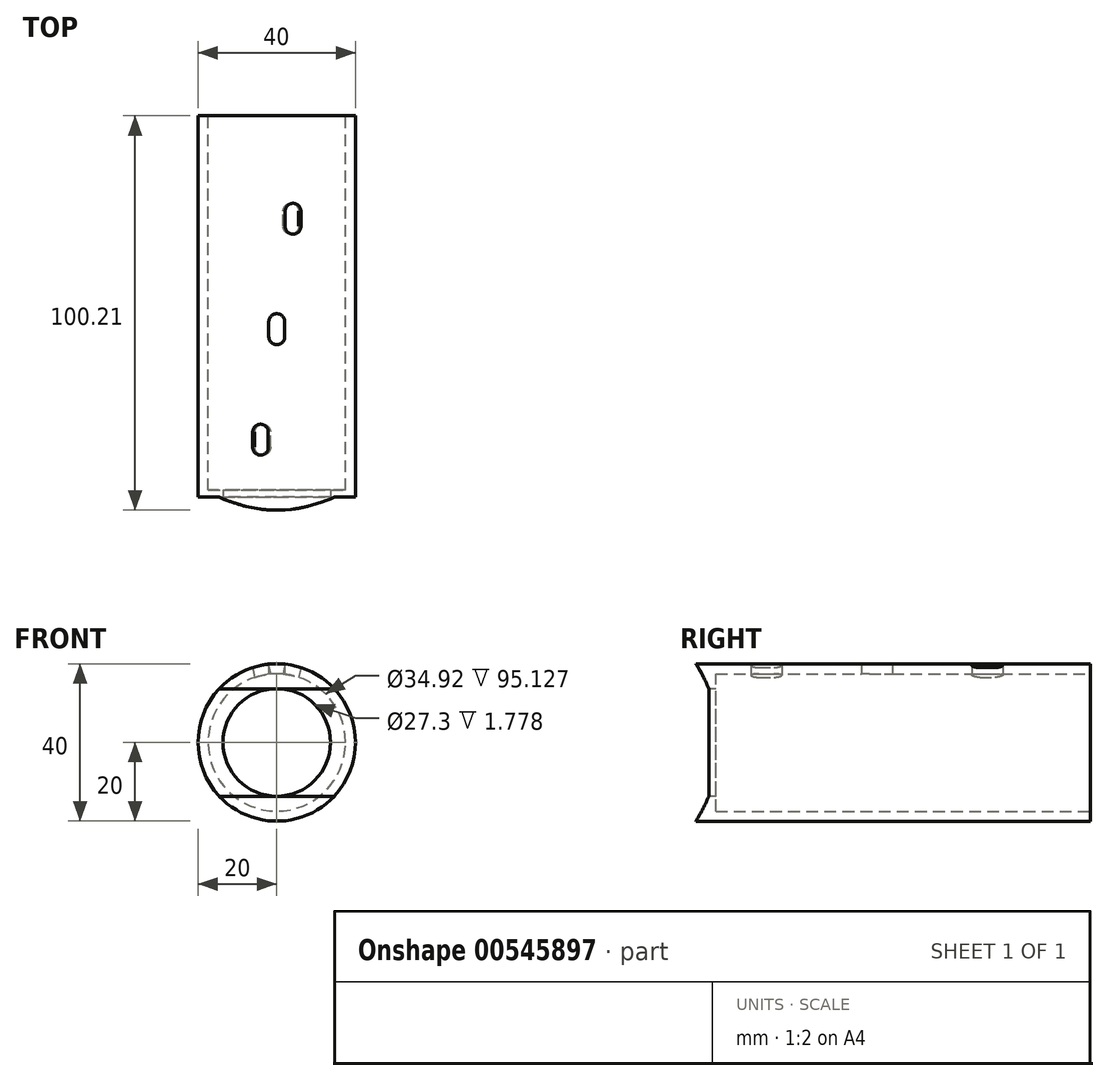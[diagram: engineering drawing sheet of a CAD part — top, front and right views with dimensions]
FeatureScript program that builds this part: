
annotation { "Feature Type Name" : "Feature", "Feature Type Description" : "" }
export const myFeature = defineFeature(function(context is Context, id is Id, definition is map)
    precondition{}
    {
        {
            var Q0;
            Q0=qCreatedBy(makeId("Front.planeOp"),FACE);
            var sketch = newSketch(context, id + "F0", { "sketchPlane" : qUnion([Q0])});
            skCircle(sketch, "E0", {"center": v(0, 0) * mm, "radius": 20 * mm});
            skCircle(sketch, "E1", {"center": v(0, 0) * mm, "radius": 17.46 * mm});
            skSolve(sketch);
        }
        {
            var Q0;
            Q0 = qSketchRegion(id + "F0", true);
            extrude(context, id + "F1", {"entities" : qUnion([Q0]), "endBound" : BoundingType.SYMMETRIC, "depth" : 95 * mm, "offsetDistance" : 25.4 * mm});
        }
        {
            var Q0;
            Q0=makeQuery(id+"F1.opExtrude","CAP_FACE",FACE,{"disambiguationData":[OSD([sQuery(id+"F0.wireOp",EDGE,"E0"),sQuery(id+"F0.wireOp",EDGE,"E1")])],"isStart":false});
            var sketch = newSketch(context, id + "F2", { "sketchPlane" : qUnion([Q0])});
            skCircle(sketch, "E2", {"center": v(0, 0) * mm, "radius": 13.65 * mm});
            skCircle(sketch, "E3.0", {"center": v(0, 0) * mm, "radius": 20 * mm});
            skCircle(sketch, "E4.0", {"center": v(0, 0) * mm, "radius": 17.46 * mm, "construction": true});
            skSolve(sketch);
        }
        {
            var Q0;
            Q0 = qSketchRegion(id + "F2", true);
            extrude(context, id + "F3", {"entities" : qUnion([Q0]), "operationType" : NewBodyOperationType.ADD, "oppositeDirection" : true, "depth" : 5.08 * mm, "offsetDistance" : 25.4 * mm});
        }
        {
            var Q0;
            Q0=qCreatedBy(makeId("Right.planeOp"),FACE);
            var sketch = newSketch(context, id + "F4", { "sketchPlane" : qUnion([Q0])});
            skLineSegment(sketch, "E5.0", {"start": v(-47.5, -20) * mm, "end": v(-47.5, -20) * mm});
            skArc(sketch, "E6", {"start": v(-44.2, 13.65) * mm, "mid": v(-45.7, 16.9) * mm, "end": v(-47.5, 20) * mm});
            skLineSegment(sketch, "E7.0", {"start": v(-42.42, -17.46) * mm, "end": v(-42.42, 17.46) * mm, "construction": true});
            skLineSegment(sketch, "E8", {"start": v(-42.42, 13.65) * mm, "end": v(-44.2, 13.65) * mm, "construction": true});
            skLineSegment(sketch, "E9", {"start": v(-44.2, 13.65) * mm, "end": v(-44.2, -13.65) * mm});
            skArc(sketch, "E10", {"start": v(-47.5, 20) * mm, "mid": v(-114.68, -3.58) * mm, "end": v(-44.2, -13.65) * mm, "construction": true});
            skLineSegment(sketch, "E11", {"start": v(-47.5, -20) * mm, "end": v(-47.5, 20) * mm});
            skArc(sketch, "E12.MirrorCS", {"start": v(-44.2, -13.65) * mm, "mid": v(-45.7, -16.9) * mm, "end": v(-47.5, -20) * mm});
            skSolve(sketch);
        }
        {
            var Q0;
            Q0 = qSketchRegion(id + "F4", true);
            extrude(context, id + "F5", {"entities" : qUnion([Q0]), "operationType" : NewBodyOperationType.REMOVE, "endBound" : BoundingType.THROUGH_ALL, "oppositeDirection" : true, "depth" : 25.4 * mm, "offsetDistance" : 25.4 * mm, "hasSecondDirection" : true, "secondDirectionBound" : SecondDirectionBoundingType.THROUGH_ALL, "secondDirectionOppositeDirection" : false, "secondDirectionDepth" : 25.4 * mm});
        }
        {
            var Q0;
            Q0=qCreatedBy(makeId("Top.planeOp"),FACE);
            var sketch = newSketch(context, id + "F6", { "sketchPlane" : qUnion([Q0])});
            skLineSegment(sketch, "E13.bottom", {"start": v(-2.03, -3.43) * mm, "end": v(2.03, -3.43) * mm, "construction": true});
            skLineSegment(sketch, "E13.top", {"start": v(-2.03, 0.38) * mm, "end": v(2.03, 0.38) * mm, "construction": true});
            skLineSegment(sketch, "E13.left", {"start": v(-2.03, -3.43) * mm, "end": v(-2.03, 0.38) * mm});
            skLineSegment(sketch, "E13.right", {"start": v(2.03, -3.43) * mm, "end": v(2.03, 0.38) * mm});
            skArc(sketch, "E14", {"start": v(-2.03, 0.38) * mm, "mid": v(0, 2.41) * mm, "end": v(2.03, 0.38) * mm});
            skArc(sketch, "E15", {"start": v(-2.03, -3.43) * mm, "mid": v(0, -5.46) * mm, "end": v(2.03, -3.43) * mm});
            skSolve(sketch);
        }
        {
            var Q0;
            Q0 = qSketchRegion(id + "F6", true);
            extrude(context, id + "F7", {"entities" : qUnion([Q0]), "operationType" : NewBodyOperationType.REMOVE, "endBound" : BoundingType.THROUGH_ALL, "depth" : 25.4 * mm, "offsetDistance" : 25.4 * mm});
        }
        {
            var Q0;
            Q0=qCreatedBy(makeId("Front.planeOp"),FACE);
            var sketch = newSketch(context, id + "F8", { "sketchPlane" : qUnion([Q0])});
            skLineSegment(sketch, "E16", {"start": v(-43.88, 9.33) * mm, "end": v(0, 0) * mm, "construction": true});
            skLineSegment(sketch, "E17", {"start": v(0, 0) * mm, "end": v(39.67, 8.43) * mm, "construction": true});
            skSolve(sketch);
        }
        {
            var Q0;
            Q0=sQuery(id+"F8.wireOp",EDGE,"E17");
            var Q1;
            Q1=qCreatedBy(makeId("Top.planeOp"),FACE);
            cPlane(context, id + "F9", {"entities" : qUnion([Q0, Q1]), "cplaneType" : CPlaneType.LINE_ANGLE, "offset" : 25.4 * mm, "angle" : 0 * degree, "width" : 152.4 * mm, "height" : 152.4 * mm});
        }
        {
            var Q0;
            Q0=qCreatedBy(id+"F9.planeOp",FACE);
            var sketch = newSketch(context, id + "F10", { "sketchPlane" : qUnion([Q0])});
            skLineSegment(sketch, "E18.bottom", {"start": v(-2.03, 31.5) * mm, "end": v(2.03, 31.5) * mm, "construction": true});
            skLineSegment(sketch, "E18.top", {"start": v(-2.03, 27.69) * mm, "end": v(2.03, 27.69) * mm, "construction": true});
            skLineSegment(sketch, "E18.left", {"start": v(-2.03, 31.5) * mm, "end": v(-2.03, 27.69) * mm});
            skLineSegment(sketch, "E18.right", {"start": v(2.03, 31.5) * mm, "end": v(2.03, 27.69) * mm});
            skArc(sketch, "E19", {"start": v(-2.03, 27.69) * mm, "mid": v(0, 25.66) * mm, "end": v(2.03, 27.69) * mm});
            skArc(sketch, "E20", {"start": v(-2.03, 31.5) * mm, "mid": v(0, 33.53) * mm, "end": v(2.03, 31.5) * mm});
            skSolve(sketch);
        }
        {
            var Q0;
            Q0 = qSketchRegion(id + "F10", true);
            extrude(context, id + "F11", {"entities" : qUnion([Q0]), "operationType" : NewBodyOperationType.REMOVE, "endBound" : BoundingType.THROUGH_ALL, "oppositeDirection" : true, "depth" : 25.4 * mm, "offsetDistance" : 25.4 * mm});
        }
        {
            var Q0;
            Q0=sQuery(id+"F8.wireOp",EDGE,"E16");
            var Q1;
            Q1=qCreatedBy(makeId("Top.planeOp"),FACE);
            cPlane(context, id + "F12", {"entities" : qUnion([Q0, Q1]), "cplaneType" : CPlaneType.LINE_ANGLE, "offset" : 25.4 * mm, "angle" : 0 * degree, "width" : 152.4 * mm, "height" : 152.4 * mm});
        }
        {
            var Q0;
            Q0=qCreatedBy(id+"F12.planeOp",FACE);
            var sketch = newSketch(context, id + "F13", { "sketchPlane" : qUnion([Q0])});
            skLineSegment(sketch, "E21.bottom", {"start": v(2.03, -24.64) * mm, "end": v(-2.03, -24.64) * mm, "construction": true});
            skLineSegment(sketch, "E21.top", {"start": v(2.03, -28.45) * mm, "end": v(-2.03, -28.45) * mm, "construction": true});
            skLineSegment(sketch, "E21.left", {"start": v(2.03, -24.64) * mm, "end": v(2.03, -28.45) * mm});
            skLineSegment(sketch, "E21.right", {"start": v(-2.03, -24.64) * mm, "end": v(-2.03, -28.45) * mm});
            skArc(sketch, "E22", {"start": v(2.03, -24.64) * mm, "mid": v(0, -22.6) * mm, "end": v(-2.03, -24.64) * mm});
            skArc(sketch, "E23", {"start": v(2.03, -28.45) * mm, "mid": v(0, -30.48) * mm, "end": v(-2.03, -28.45) * mm});
            skSolve(sketch);
        }
        {
            var Q0;
            Q0 = qSketchRegion(id + "F13", true);
            extrude(context, id + "F14", {"entities" : qUnion([Q0]), "operationType" : NewBodyOperationType.REMOVE, "endBound" : BoundingType.THROUGH_ALL, "oppositeDirection" : true, "depth" : 25.4 * mm, "offsetDistance" : 25.4 * mm});
        }
        {
            var Q0;
            Q0=makeQuery(id+"F1.opExtrude","CAP_FACE",FACE,{"disambiguationData":[OSD([sQuery(id+"F0.wireOp",EDGE,"E0"),sQuery(id+"F0.wireOp",EDGE,"E1")])],"isStart":true});
            var sketch = newSketch(context, id + "F15", { "sketchPlane" : qUnion([Q0])});
            skCircle(sketch, "E24.0", {"center": v(0, 0) * mm, "radius": 20 * mm});
            skCircle(sketch, "E25.0", {"center": v(0, 0) * mm, "radius": 17.46 * mm});
            skSolve(sketch);
        }
        {
            var Q0;
            Q0 = qSketchRegion(id + "F15", true);
            extrude(context, id + "F16", {"entities" : qUnion([Q0]), "operationType" : NewBodyOperationType.ADD, "depth" : 5.2 * mm, "offsetDistance" : 25.4 * mm});
        }
    });
